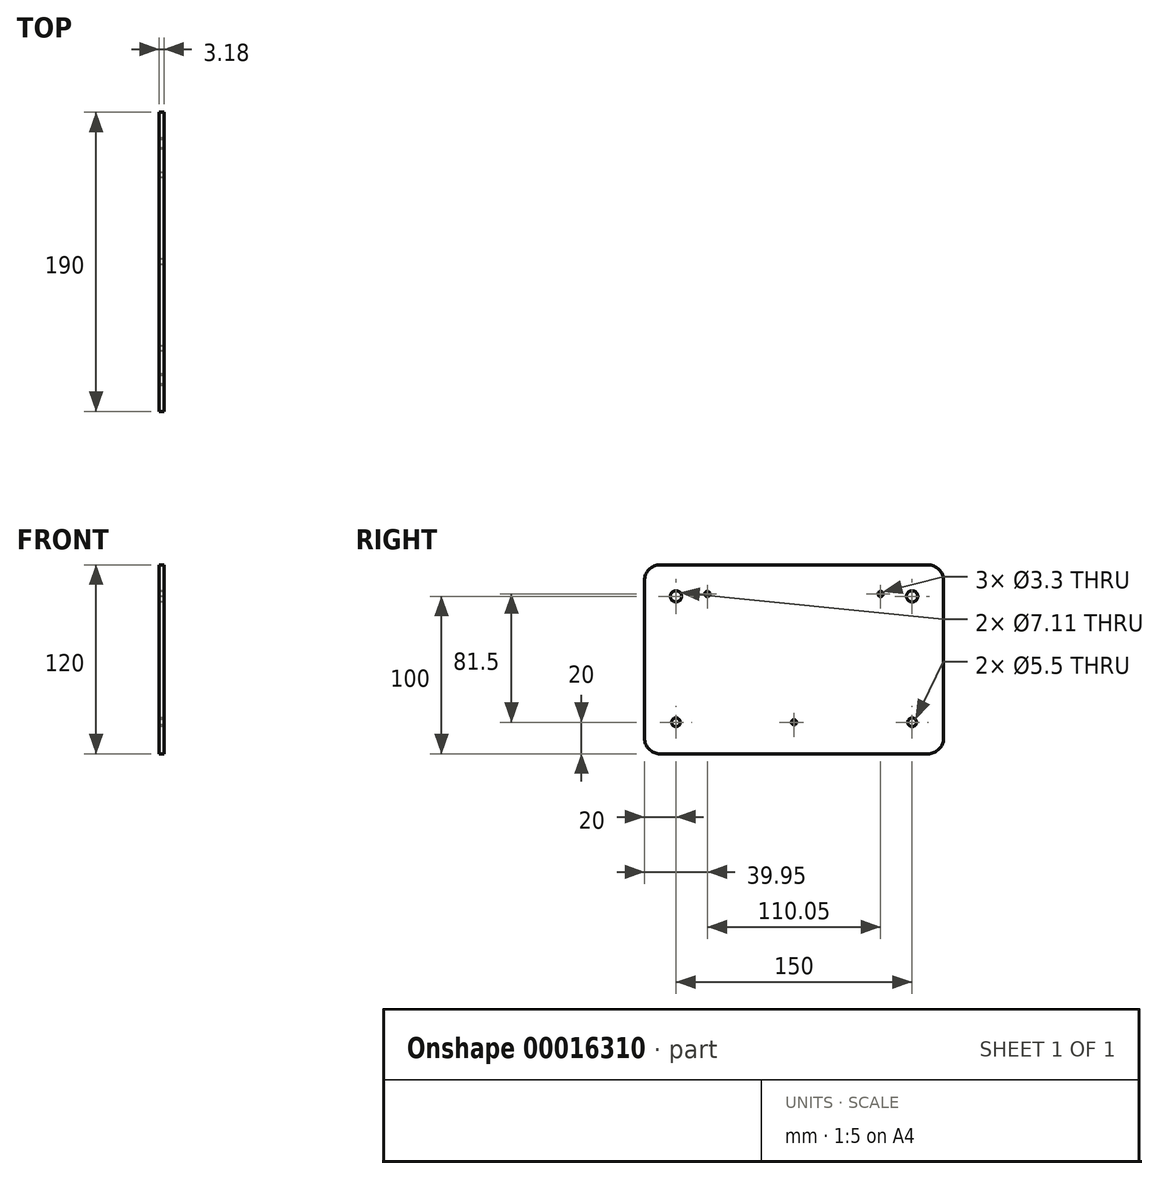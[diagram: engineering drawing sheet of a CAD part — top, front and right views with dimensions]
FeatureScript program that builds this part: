
annotation { "Feature Type Name" : "Feature", "Feature Type Description" : "" }
export const myFeature = defineFeature(function(context is Context, id is Id, definition is map)
    precondition{}
    {
        {
            var Q0;
            Q0=qCreatedBy(makeId("Right.planeOp"),FACE);
            var sketch = newSketch(context, id + "F0", { "sketchPlane" : qUnion([Q0])});
            skLineSegment(sketch, "E0", {"start": v(-85, -20) * mm, "end": v(85, -20) * mm});
            skLineSegment(sketch, "E1", {"start": v(95, -10) * mm, "end": v(95, 90) * mm});
            skLineSegment(sketch, "E2", {"start": v(85, 100) * mm, "end": v(-85, 100) * mm});
            skLineSegment(sketch, "E3", {"start": v(-95, 90) * mm, "end": v(-95, -10) * mm});
            skLineSegment(sketch, "E4", {"start": v(0, 100) * mm, "end": v(0, -20) * mm, "construction": true});
            skLineSegment(sketch, "E5", {"start": v(-95, 40) * mm, "end": v(95, 40) * mm, "construction": true});
            skLineSegment(sketch, "E6", {"start": v(0, -20) * mm, "end": v(0, 0) * mm, "construction": true});
            skLineSegment(sketch, "E7", {"start": v(0, 0) * mm, "end": v(55, 0) * mm, "construction": true});
            skLineSegment(sketch, "E8", {"start": v(55, 0) * mm, "end": v(55, 81.5) * mm, "construction": true});
            skLineSegment(sketch, "E9", {"start": v(0, 0) * mm, "end": v(-55.05, 0) * mm, "construction": true});
            skLineSegment(sketch, "E10", {"start": v(-55.05, 0) * mm, "end": v(-55.05, 81.5) * mm, "construction": true});
            skCircle(sketch, "E11", {"center": v(-55.05, 81.5) * mm, "radius": 1.65 * mm});
            skCircle(sketch, "E12", {"center": v(55, 81.5) * mm, "radius": 1.65 * mm});
            skCircle(sketch, "E13", {"center": v(0, 0) * mm, "radius": 1.65 * mm});
            skLineSegment(sketch, "E14.rect.bottom", {"start": v(-155.15, 10) * mm, "end": v(155.15, 10) * mm, "construction": true});
            skLineSegment(sketch, "E14.rect.top", {"start": v(-155.15, 70) * mm, "end": v(155.15, 70) * mm, "construction": true});
            skLineSegment(sketch, "E14.rect.left", {"start": v(-155.15, 10) * mm, "end": v(-155.15, 70) * mm, "construction": true});
            skLineSegment(sketch, "E14.rect.right", {"start": v(155.15, 10) * mm, "end": v(155.15, 70) * mm, "construction": true});
            skPoint(sketch, "E14.rect.middle", {"position": v(0, 40) * mm});
            skLineSegment(sketch, "E15", {"start": v(-95, 80) * mm, "end": v(-75, 80) * mm, "construction": true});
            skLineSegment(sketch, "E16", {"start": v(-75, 80) * mm, "end": v(-75, 70) * mm, "construction": true});
            skLineSegment(sketch, "E17", {"start": v(95, 80) * mm, "end": v(75, 80) * mm, "construction": true});
            skLineSegment(sketch, "E18", {"start": v(75, 80) * mm, "end": v(75, 70) * mm, "construction": true});
            skLineSegment(sketch, "E19", {"start": v(95, 0) * mm, "end": v(75, 0) * mm, "construction": true});
            skLineSegment(sketch, "E20", {"start": v(75, 0) * mm, "end": v(75, 10) * mm, "construction": true});
            skLineSegment(sketch, "E21", {"start": v(-95, 0) * mm, "end": v(-75, 0) * mm, "construction": true});
            skLineSegment(sketch, "E22", {"start": v(-75, 0) * mm, "end": v(-75, 10) * mm, "construction": true});
            skCircle(sketch, "E23", {"center": v(75, 80) * mm, "radius": 3.56 * mm});
            skCircle(sketch, "E24", {"center": v(75, 0) * mm, "radius": 2.75 * mm});
            skCircle(sketch, "E25", {"center": v(-75, 0) * mm, "radius": 2.75 * mm});
            skCircle(sketch, "E26", {"center": v(-75, 80) * mm, "radius": 3.56 * mm});
            skPoint(sketch, "E27.visualSharp", {"position": v(-95, 100) * mm});
            skArc(sketch, "E27.filletArc", {"start": v(-85, 100) * mm, "mid": v(-92.07, 97.07) * mm, "end": v(-95, 90) * mm});
            skPoint(sketch, "E28.visualSharp", {"position": v(95, 100) * mm});
            skArc(sketch, "E28.filletArc", {"start": v(95, 90) * mm, "mid": v(92.07, 97.07) * mm, "end": v(85, 100) * mm});
            skPoint(sketch, "E29.visualSharp", {"position": v(95, -20) * mm});
            skArc(sketch, "E29.filletArc", {"start": v(85, -20) * mm, "mid": v(92.07, -17.07) * mm, "end": v(95, -10) * mm});
            skPoint(sketch, "E30.visualSharp", {"position": v(-95, -20) * mm});
            skArc(sketch, "E30.filletArc", {"start": v(-95, -10) * mm, "mid": v(-92.07, -17.07) * mm, "end": v(-85, -20) * mm});
            skCircle(sketch, "E31", {"center": v(-75, 0) * mm, "radius": 12 * mm, "construction": true});
            skLineSegment(sketch, "E32", {"start": v(-75, 80) * mm, "end": v(-75, 100) * mm, "construction": true});
            skLineSegment(sketch, "E33", {"start": v(75, 80) * mm, "end": v(95, 80) * mm, "construction": true});
            skSolve(sketch);
        }
        {
            var Q0;
            Q0=makeQuery(id+"F0.imprint","IMPRINT",FACE,{"disambiguationData":[TD([[makeQuery(id+"F0.imprint","IMPRINT",EDGE,{"derivedFrom":sQuery(id+"F0.wireOp",EDGE,"E0")}),1.0]])]});
            extrude(context, id + "F1", {"entities" : qUnion([Q0]), "depth" : 3.17 * mm});
        }
    });
